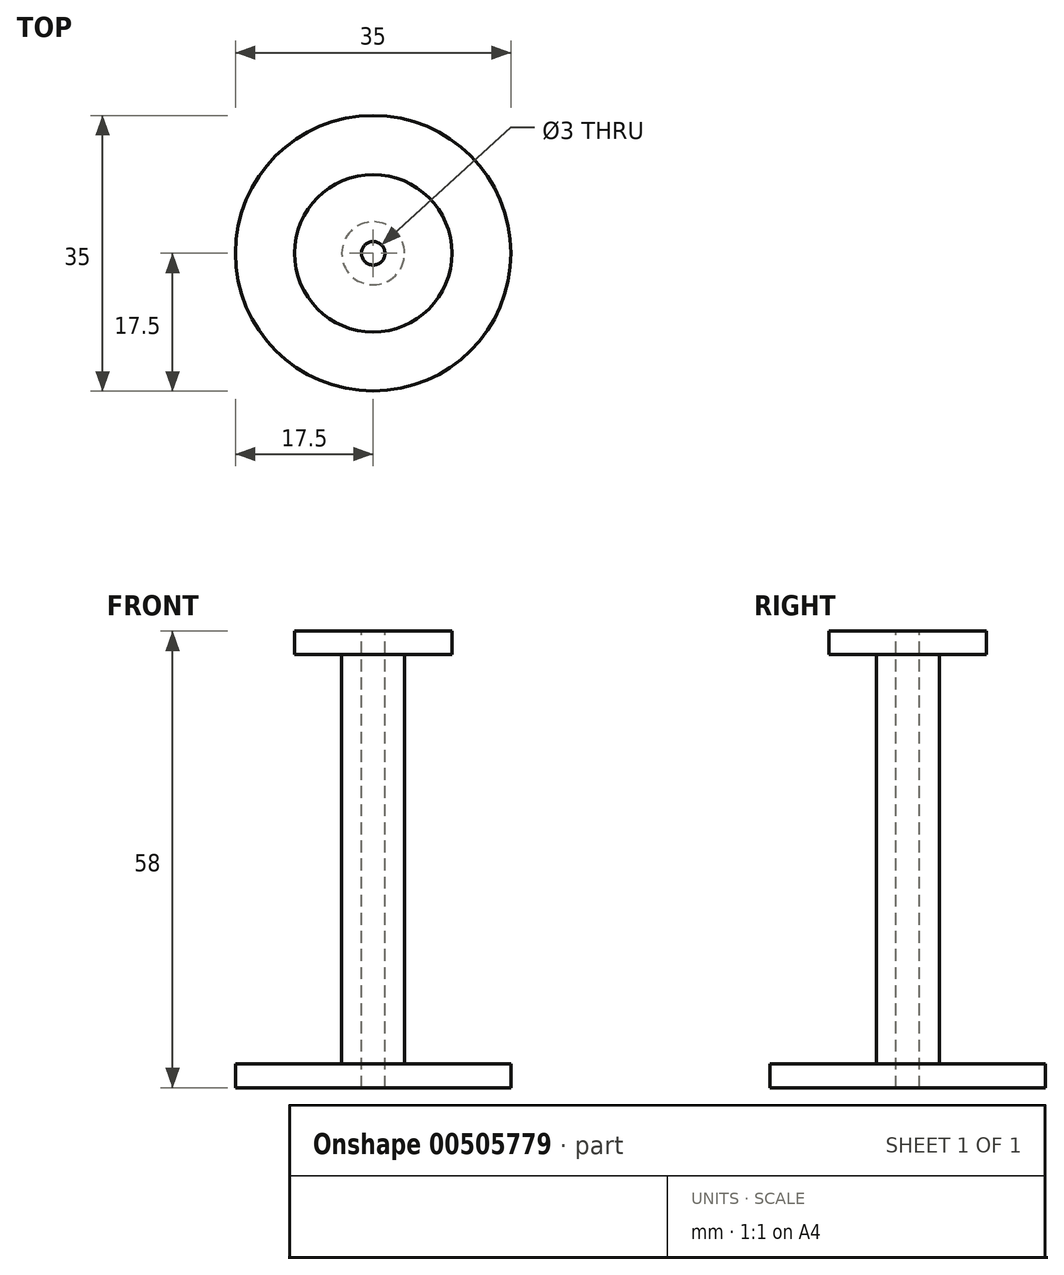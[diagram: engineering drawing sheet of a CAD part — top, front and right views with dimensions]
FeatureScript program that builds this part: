
annotation { "Feature Type Name" : "Feature", "Feature Type Description" : "" }
export const myFeature = defineFeature(function(context is Context, id is Id, definition is map)
    precondition{}
    {
        {
            var Q0;
            Q0=qCreatedBy(makeId("Top.planeOp"),FACE);
            var sketch = newSketch(context, id + "F0", { "sketchPlane" : qUnion([Q0])});
            skCircle(sketch, "E0", {"center": v(0, 0) * mm, "radius": 4 * mm});
            skCircle(sketch, "E1", {"center": v(0, 0) * mm, "radius": 17.5 * mm});
            skSolve(sketch);
        }
        {
            var Q0;
            Q0=makeQuery(id+"F0.imprint","IMPRINT",FACE,{"disambiguationData":[TD([[makeQuery(id+"F0.imprint","IMPRINT",EDGE,{"derivedFrom":sQuery(id+"F0.wireOp",EDGE,"E0")}),-1.0]])]});
            var Q1;
            Q1=makeQuery(id+"F0.imprint","IMPRINT",FACE,{"disambiguationData":[TD([[makeQuery(id+"F0.imprint","IMPRINT",EDGE,{"derivedFrom":sQuery(id+"F0.wireOp",EDGE,"E0")}),1.0]])]});
            extrude(context, id + "F1", {"entities" : qUnion([Q0, Q1]), "depth" : 3 * mm});
        }
        {
            var Q0;
            Q0=makeQuery(id+"F0.imprint","IMPRINT",FACE,{"disambiguationData":[TD([[makeQuery(id+"F0.imprint","IMPRINT",EDGE,{"derivedFrom":sQuery(id+"F0.wireOp",EDGE,"E0")}),1.0]])]});
            extrude(context, id + "F2", {"entities" : qUnion([Q0]), "operationType" : NewBodyOperationType.ADD, "depth" : 55 * mm});
        }
        {
            var Q0;
            Q0=makeQuery(id+"F2.opExtrude","CAP_FACE",FACE,{"disambiguationData":[OSD([sQuery(id+"F0.wireOp",EDGE,"E0")])],"isStart":false});
            var sketch = newSketch(context, id + "F3", { "sketchPlane" : qUnion([Q0])});
            skCircle(sketch, "E2", {"center": v(0, 0) * mm, "radius": 10 * mm});
            skSolve(sketch);
        }
        {
            var Q0;
            Q0=makeQuery(id+"F3.imprint","IMPRINT",FACE,{"disambiguationData":[TD([[makeQuery(id+"F3.imprint","IMPRINT",EDGE,{"derivedFrom":sQuery(id+"F3.wireOp",EDGE,"E2")}),1.0]])]});
            var Q1;
            Q1=makeQuery(id+"F3.imprint","IMPRINT",FACE,{"disambiguationData":[TD([[makeQuery(id+"F3.imprint","IMPRINT",EDGE,{"derivedFrom":makeQuery(id+"F2.opExtrude","CAP_EDGE",EDGE,{"disambiguationData":[OSD([sQuery(id+"F0.wireOp",EDGE,"E0")])],"isStart":false})}),1.0]])]});
            extrude(context, id + "F4", {"entities" : qUnion([Q0, Q1]), "operationType" : NewBodyOperationType.ADD, "depth" : 3 * mm});
        }
        {
            var Q0;
            Q0=makeQuery(id+"F4.opExtrude","CAP_FACE",FACE,{"disambiguationData":[OSD([sQuery(id+"F3.wireOp",EDGE,"E2")])],"isStart":false});
            var sketch = newSketch(context, id + "F5", { "sketchPlane" : qUnion([Q0])});
            skCircle(sketch, "E3", {"center": v(0, 0) * mm, "radius": 1.5 * mm});
            skSolve(sketch);
        }
        {
            var Q0;
            Q0=makeQuery(id+"F5.imprint","IMPRINT",FACE,{"disambiguationData":[TD([[makeQuery(id+"F5.imprint","IMPRINT",EDGE,{"derivedFrom":sQuery(id+"F5.wireOp",EDGE,"E3")}),1.0]])]});
            var Q1;
            Q1=sQuery(id+"F5.wireOp",EDGE,"E3");
            extrude(context, id + "F6", {"entities" : qUnion([Q0]), "operationType" : NewBodyOperationType.REMOVE, "surfaceEntities" : qUnion([Q1]), "endBound" : BoundingType.THROUGH_ALL, "oppositeDirection" : true, "depth" : 25 * mm});
        }
    });
